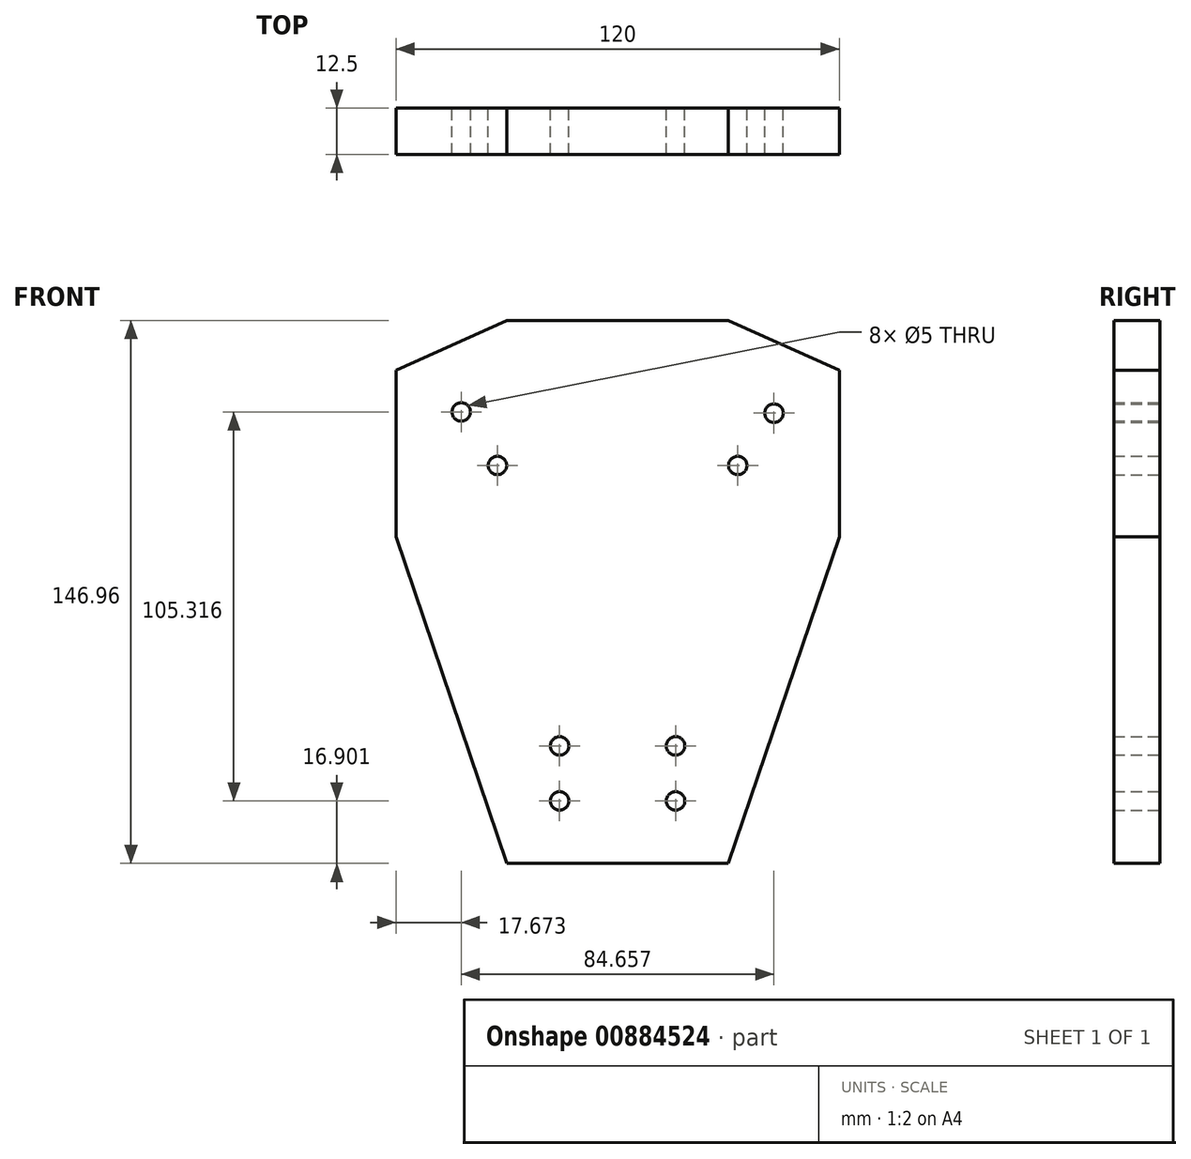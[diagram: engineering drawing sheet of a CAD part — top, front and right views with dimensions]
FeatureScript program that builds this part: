
annotation { "Feature Type Name" : "Feature", "Feature Type Description" : "" }
export const myFeature = defineFeature(function(context is Context, id is Id, definition is map)
    precondition{}
    {
        {
            var Q0;
            Q0=qCreatedBy(makeId("Front.planeOp"),FACE);
            var sketch = newSketch(context, id + "F0", { "sketchPlane" : qUnion([Q0])});
            skPoint(sketch, "E0.middle", {"position": v(0, 0) * mm});
            skLineSegment(sketch, "E1.bottom", {"start": v(-30, 73.48) * mm, "end": v(30, 73.48) * mm});
            skLineSegment(sketch, "E1.top", {"start": v(-30, -73.48) * mm, "end": v(30, -73.48) * mm});
            skLineSegment(sketch, "E2", {"start": v(-60, 60) * mm, "end": v(-30, 73.48) * mm});
            skLineSegment(sketch, "E3", {"start": v(30, 73.48) * mm, "end": v(60, 60) * mm});
            skPoint(sketch, "E4", {"position": v(-60, 14.89) * mm});
            skLineSegment(sketch, "E5", {"start": v(-30, -73.48) * mm, "end": v(-60, 14.89) * mm});
            skLineSegment(sketch, "E6", {"start": v(30, -73.48) * mm, "end": v(60, 14.89) * mm});
            skLineSegment(sketch, "E7", {"start": v(-60, 60) * mm, "end": v(-60, 14.89) * mm});
            skLineSegment(sketch, "E8", {"start": v(60, 60) * mm, "end": v(60, 14.89) * mm});
            skLineSegment(sketch, "E9", {"start": v(35.74, -56.58) * mm, "end": v(40.8, -41.68) * mm});
            skCircle(sketch, "E10", {"center": v(-15.7, -41.68) * mm, "radius": 2.5 * mm});
            skCircle(sketch, "E11", {"center": v(-15.7, -56.58) * mm, "radius": 2.5 * mm});
            skCircle(sketch, "E12", {"center": v(15.7, -56.58) * mm, "radius": 2.5 * mm});
            skCircle(sketch, "E13", {"center": v(15.7, -41.68) * mm, "radius": 2.5 * mm});
            skCircle(sketch, "E14", {"center": v(-42.33, 48.74) * mm, "radius": 2.5 * mm});
            skCircle(sketch, "E15", {"center": v(-32.53, 34.25) * mm, "radius": 2.5 * mm});
            skCircle(sketch, "E16", {"center": v(32.53, 34.25) * mm, "radius": 2.5 * mm});
            skCircle(sketch, "E17", {"center": v(42.33, 48.4) * mm, "radius": 2.5 * mm});
            skSolve(sketch);
        }
        {
            var Q0;
            Q0 = qSketchRegion(id + "F0", true);
            extrude(context, id + "F1", {"entities" : qUnion([Q0]), "depth" : 12.5 * mm, "offsetDistance" : 25 * mm});
        }
    });
